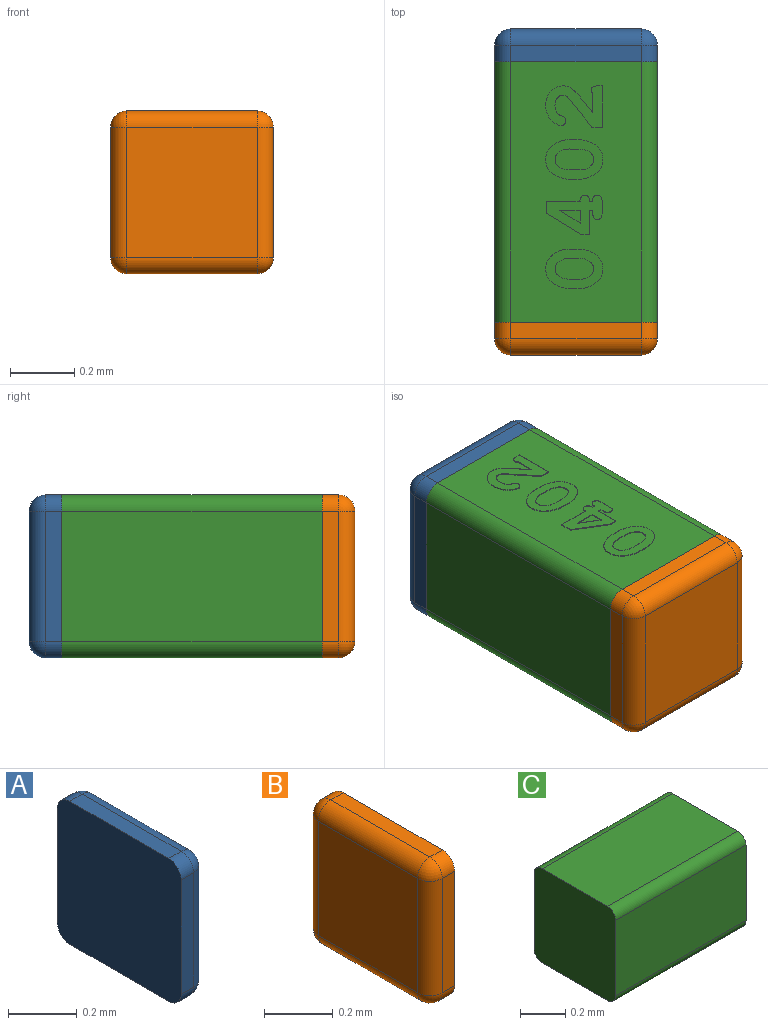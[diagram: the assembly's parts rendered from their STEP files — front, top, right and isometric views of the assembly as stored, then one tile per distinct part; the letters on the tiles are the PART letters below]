
ASSEMBLY  parts=3 mates=2
PART A: 18 faces, bbox 0.1x0.5x0.5 mm
  f0: plane 0.51x0.51mm, normal (-1,0,0), area 0.3mm2, adj f1,f2,f3,f4,f5,f6,f7,f8
  f1: plane 0.41x0.05mm, normal (0,0,1), area 0mm2, adj f0,f2,f8,f9
  f2: cylinder r=0.05mm len=0.05mm, axis (-1,0,0), area 0mm2, adj f0,f1,f3,f10
  f3: plane 0.41x0.05mm, normal (0,1,0), area 0mm2, adj f0,f2,f4,f11
  f4: cylinder r=0.05mm len=0.05mm, axis (-1,0,0), area 0mm2, adj f0,f3,f5,f12
  f5: plane 0.41x0.05mm, normal (0,0,-1), area 0mm2, adj f0,f4,f6,f13
  f6: cylinder r=0.05mm len=0.05mm, axis (-1,0,0), area 0mm2, adj f0,f5,f7,f14
  f7: plane 0.41x0.05mm, normal (0,-1,0), area 0mm2, adj f0,f6,f8,f15
  f8: cylinder r=0.05mm len=0.05mm, axis (-1,0,0), area 0mm2, adj f0,f1,f7,f16
  f9: cylinder r=0.05mm len=0.41mm, axis (0,1,0), area 0mm2, adj f1,f10,f16,f17
  f10: sphere r=0.05mm, area 0mm2, adj f2,f9,f11
  f11: cylinder r=0.05mm len=0.41mm, axis (0,0,-1), area 0mm2, adj f3,f10,f12,f17
  f12: sphere r=0.05mm, area 0mm2, adj f4,f11,f13
  f13: cylinder r=0.05mm len=0.41mm, axis (0,-1,0), area 0mm2, adj f5,f12,f14,f17
  f14: sphere r=0.05mm, area 0mm2, adj f6,f13,f15
  f15: cylinder r=0.05mm len=0.41mm, axis (0,0,1), area 0mm2, adj f7,f14,f16,f17
  f16: sphere r=0.05mm, area 0mm2, adj f8,f9,f15
  f17: plane 0.41x0.41mm, normal (1,0,0), area 0.2mm2, adj f9,f11,f13,f15
PART B: 18 faces, bbox 0.1x0.5x0.5 mm
  f0: plane 0.51x0.51mm, normal (1,0,0), area 0.3mm2, adj f1,f2,f3,f4,f5,f6,f7,f8
  f1: cylinder r=0.05mm len=0.05mm, axis (1,0,0), area 0mm2, adj f0,f2,f8,f9
  f2: plane 0.41x0.05mm, normal (0,1,0), area 0mm2, adj f0,f1,f3,f10
  f3: cylinder r=0.05mm len=0.05mm, axis (1,0,0), area 0mm2, adj f0,f2,f4,f11
  f4: plane 0.41x0.05mm, normal (0,0,-1), area 0mm2, adj f0,f3,f5,f12
  f5: cylinder r=0.05mm len=0.05mm, axis (1,0,0), area 0mm2, adj f0,f4,f6,f13
  f6: plane 0.41x0.05mm, normal (0,-1,0), area 0mm2, adj f0,f5,f7,f14
  f7: cylinder r=0.05mm len=0.05mm, axis (1,0,0), area 0mm2, adj f0,f6,f8,f15
  f8: plane 0.41x0.05mm, normal (0,0,1), area 0mm2, adj f0,f1,f7,f16
  f9: sphere r=0.05mm, area 0mm2, adj f1,f10,f16
  f10: cylinder r=0.05mm len=0.41mm, axis (0,0,-1), area 0mm2, adj f2,f9,f11,f17
  f11: sphere r=0.05mm, area 0mm2, adj f3,f10,f12
  f12: cylinder r=0.05mm len=0.41mm, axis (0,-1,0), area 0mm2, adj f4,f11,f13,f17
  f13: sphere r=0.05mm, area 0mm2, adj f5,f12,f14
  f14: cylinder r=0.05mm len=0.41mm, axis (0,0,1), area 0mm2, adj f6,f13,f15,f17
  f15: sphere r=0.05mm, area 0mm2, adj f7,f14,f16
  f16: cylinder r=0.05mm len=0.41mm, axis (0,1,0), area 0mm2, adj f8,f9,f15,f17
  f17: plane 0.41x0.41mm, normal (-1,0,0), area 0.2mm2, adj f10,f12,f14,f16
PART C: 84 faces, bbox 0.8x0.5x0.5 mm
  f0: plane 0.81x0.41mm, normal (0,-1,0), area 0.3mm2, adj f1,f2,f3,f4
  f1: plane 0.51x0.51mm, normal (1,0,0), area 0.3mm2, adj f0,f2,f4,f5,f6,f7,f8,f9
  f2: cylinder r=0.05mm len=0.81mm, axis (1,0,0), area 0.1mm2, adj f0,f1,f3,f9
  f3: plane 0.51x0.51mm, normal (-1,0,0), area 0.3mm2, adj f0,f2,f4,f5,f6,f7,f8,f9
  f4: cylinder r=0.05mm len=0.81mm, axis (-1,0,0), area 0.1mm2, adj f0,f1,f3,f5
  f5: plane 0.81x0.41mm, normal (0,0,-1), area 0.3mm2, adj f1,f3,f4,f6
  f6: cylinder r=0.05mm len=0.81mm, axis (1,0,0), area 0.1mm2, adj f1,f3,f5,f7
  f7: plane 0.81x0.41mm, normal (0,1,0), area 0.3mm2, adj f1,f3,f6,f8,f10,f11,f12,f13
  f8: cylinder r=0.05mm len=0.81mm, axis (-1,0,0), area 0.1mm2, adj f1,f3,f7,f9
  f9: plane 0.81x0.41mm, normal (0,0,1), area 0.3mm2, adj f1,f2,f3,f8
  f10: plane 0.01x0mm, normal (0,0,-1), area 0mm2, adj f7,f11,f24,f54
  f11: extruded ~0.02x0.01mm, area 0mm2, adj f7,f10,f12,f54
  f12: bspline ~0.02x0.01mm, area 0mm2, adj f7,f11,f13,f54
  f13: plane 0.04x0mm, normal (0,0,1), area 0mm2, adj f7,f12,f14,f54
  f14: extruded ~0.02x0.01mm, area 0mm2, adj f7,f13,f15,f54
  f15: sphere r=0.02mm, area 0mm2, adj f7,f14,f16,f54
  f16: plane 0.01x0mm, normal (1,0,0), area 0mm2, adj f7,f15,f17,f54
  f17: extruded ~0.02x0.01mm, area 0mm2, adj f7,f16,f18,f54
  f18: sphere r=0.02mm, area 0mm2, adj f7,f17,f19,f54
  f19: plane 0.1x0mm, normal (1,0,0), area 0mm2, adj f7,f18,f20,f54
  f20: plane 0.04x0mm, normal (0,0,-1), area 0mm2, adj f7,f19,f21,f54
  f21: plane 0.11x0.07mm, normal (-0.85,0,-0.52), area 0mm2, adj f7,f20,f22,f54
  f22: plane 0.02x0mm, normal (-1,0,0), area 0mm2, adj f7,f21,f23,f54
  f23: plane 0.08x0mm, normal (0,0,1), area 0mm2, adj f7,f22,f24,f54
  f24: plane 0.01x0mm, normal (-1,0,0), area 0mm2, adj f7,f10,f23,f54
  f25: plane 0.03x0mm, normal (1,0,0), area 0mm2, adj f7,f26,f30,f55
  f26: extruded ~0.07x0.06mm, area 0mm2, adj f7,f25,f27,f55
  f27: extruded ~0.07x0.06mm, area 0mm2, adj f7,f26,f28,f55
  f28: plane 0.03x0mm, normal (-1,0,0), area 0mm2, adj f7,f27,f29,f55
  f29: extruded ~0.07x0.06mm, area 0mm2, adj f7,f28,f30,f55
  f30: extruded ~0.07x0.06mm, area 0mm2, adj f7,f25,f29,f55
  f31: plane 0.03x0mm, normal (1,0,0), area 0mm2, adj f7,f32,f36,f56
  f32: extruded ~0.07x0.06mm, area 0mm2, adj f7,f31,f33,f56
  f33: extruded ~0.07x0.06mm, area 0mm2, adj f7,f32,f34,f56
  f34: plane 0.03x0mm, normal (-1,0,0), area 0mm2, adj f7,f33,f35,f56
  f35: extruded ~0.07x0.06mm, area 0mm2, adj f7,f34,f36,f56
  f36: extruded ~0.07x0.06mm, area 0mm2, adj f7,f31,f35,f56
  f37: cylinder r=0.01mm len=0.01mm, axis (0,-1,0), area 0mm2, adj f7,f38,f53,f57
  f38: cylinder r=0.03mm len=0.01mm, axis (0,1,0), area 0mm2, adj f7,f37,f39,f57
  f39: cylinder r=0.04mm len=0.03mm, axis (0,1,0), area 0mm2, adj f7,f38,f40,f57
  f40: extruded ~0.03x0.02mm, area 0mm2, adj f7,f39,f41,f57
  f41: cylinder r=0.03mm len=0.02mm, axis (0,1,0), area 0mm2, adj f7,f40,f42,f57
  f42: extruded ~0.09x0.08mm, area 0mm2, adj f7,f41,f43,f57
  f43: plane 0.03x0mm, normal (-1,0,0), area 0mm2, adj f7,f42,f44,f57
  f44: plane 0.13x0mm, normal (0,0,1), area 0mm2, adj f7,f43,f45,f57
  f45: plane 0.01x0mm, normal (1,0,0), area 0mm2, adj f7,f44,f46,f57
  f46: extruded ~0.02x0.01mm, area 0mm2, adj f7,f45,f47,f57
  f47: cylinder r=0.02mm len=0.01mm, axis (0,-1,0), area 0mm2, adj f7,f46,f48,f57
  f48: plane 0.06x0mm, normal (0,0,-1), area 0mm2, adj f7,f47,f49,f57
  f49: plane 0.06x0.05mm, normal (0.62,0,0.78), area 0mm2, adj f7,f48,f50,f57
  f50: extruded ~0.05x0.03mm, area 0mm2, adj f7,f49,f51,f57
  f51: extruded ~0.06x0.05mm, area 0mm2, adj f7,f50,f52,f57
  f52: extruded ~0.06x0.05mm, area 0mm2, adj f7,f51,f53,f57
  f53: cylinder r=0.02mm len=0.02mm, axis (0,-1,0), area 0mm2, adj f7,f37,f52,f57
  f54: plane 0.17x0.12mm, normal (0,1,0), area 0mm2, adj f10,f11,f12,f13,f14,f15,f16,f17
  f55: plane 0.18x0.12mm, normal (0,1,0), area 0mm2, adj f25,f26,f27,f28,f29,f30,f61,f62
  f56: plane 0.18x0.12mm, normal (0,1,0), area 0mm2, adj f31,f32,f33,f34,f35,f36,f71,f72
  f57: plane 0.18x0.13mm, normal (0,1,0), area 0mm2, adj f37,f38,f39,f40,f41,f42,f43,f44
  f58: plane 0.04x0mm, normal (0,0,-1), area 0mm2, adj f54,f59,f60,f81
  f59: plane 0.07x0mm, normal (-1,0,0), area 0mm2, adj f54,f58,f60,f81
  f60: plane 0.07x0.04mm, normal (0.85,0,0.52), area 0mm2, adj f54,f58,f59,f81
  f61: cylinder r=0.06mm len=0.04mm, axis (0,1,0), area 0mm2, adj f55,f62,f70,f82
  f62: cylinder r=0.02mm len=0.02mm, axis (0,1,0), area 0mm2, adj f55,f61,f63,f82
  f63: cylinder r=0.03mm len=0.02mm, axis (0,1,0), area 0mm2, adj f55,f62,f64,f82
  f64: cylinder r=0.05mm len=0.04mm, axis (0,1,0), area 0mm2, adj f55,f63,f65,f82
  f65: plane 0.03x0mm, normal (-1,0,0), area 0mm2, adj f55,f64,f66,f82
  f66: cylinder r=0.06mm len=0.04mm, axis (0,1,0), area 0mm2, adj f55,f65,f67,f82
  f67: cylinder r=0.02mm len=0.02mm, axis (0,1,0), area 0mm2, adj f55,f66,f68,f82
  f68: cylinder r=0.03mm len=0.02mm, axis (0,1,0), area 0mm2, adj f55,f67,f69,f82
  f69: cylinder r=0.05mm len=0.04mm, axis (0,1,0), area 0mm2, adj f55,f68,f70,f82
  f70: plane 0.03x0mm, normal (1,0,0), area 0mm2, adj f55,f61,f69,f82
  f71: cylinder r=0.06mm len=0.04mm, axis (0,1,0), area 0mm2, adj f56,f72,f80,f83
  f72: cylinder r=0.02mm len=0.02mm, axis (0,1,0), area 0mm2, adj f56,f71,f73,f83
  f73: cylinder r=0.03mm len=0.02mm, axis (0,1,0), area 0mm2, adj f56,f72,f74,f83
  f74: cylinder r=0.05mm len=0.04mm, axis (0,1,0), area 0mm2, adj f56,f73,f75,f83
  f75: plane 0.03x0mm, normal (-1,0,0), area 0mm2, adj f56,f74,f76,f83
  f76: cylinder r=0.06mm len=0.04mm, axis (0,1,0), area 0mm2, adj f56,f75,f77,f83
  f77: cylinder r=0.02mm len=0.02mm, axis (0,1,0), area 0mm2, adj f56,f76,f78,f83
  f78: cylinder r=0.03mm len=0.02mm, axis (0,1,0), area 0mm2, adj f56,f77,f79,f83
  f79: cylinder r=0.05mm len=0.04mm, axis (0,1,0), area 0mm2, adj f56,f78,f80,f83
  f80: plane 0.03x0mm, normal (1,0,0), area 0mm2, adj f56,f71,f79,f83
  f81: plane 0.07x0.04mm, normal (0,1,0), area 0mm2, adj f58,f59,f60
  f82: plane 0.12x0.07mm, normal (0,1,0), area 0mm2, adj f61,f62,f63,f64,f65,f66,f67,f68
  f83: plane 0.12x0.07mm, normal (0,1,0), area 0mm2, adj f71,f72,f73,f74,f75,f76,f77,f78
PLACE A rot(axis=(0.58,0.58,0.58),120deg) t=(6.07,-9.02,0)mm
PLACE B rot(axis=(0.58,0.58,0.58),120deg) t=(6.07,-9.02,0)mm
PLACE C rot(axis=(0.58,0.58,0.58),120deg) t=(6.07,-9.02,0)mm
MATE fastened A.f0 <-> C.f1  axis (0,-1,0) through (6.07,-8.61,0.25)mm
MATE fastened B.f0 <-> C.f3  axis (0,1,0) through (6.07,-9.42,0.25)mm
